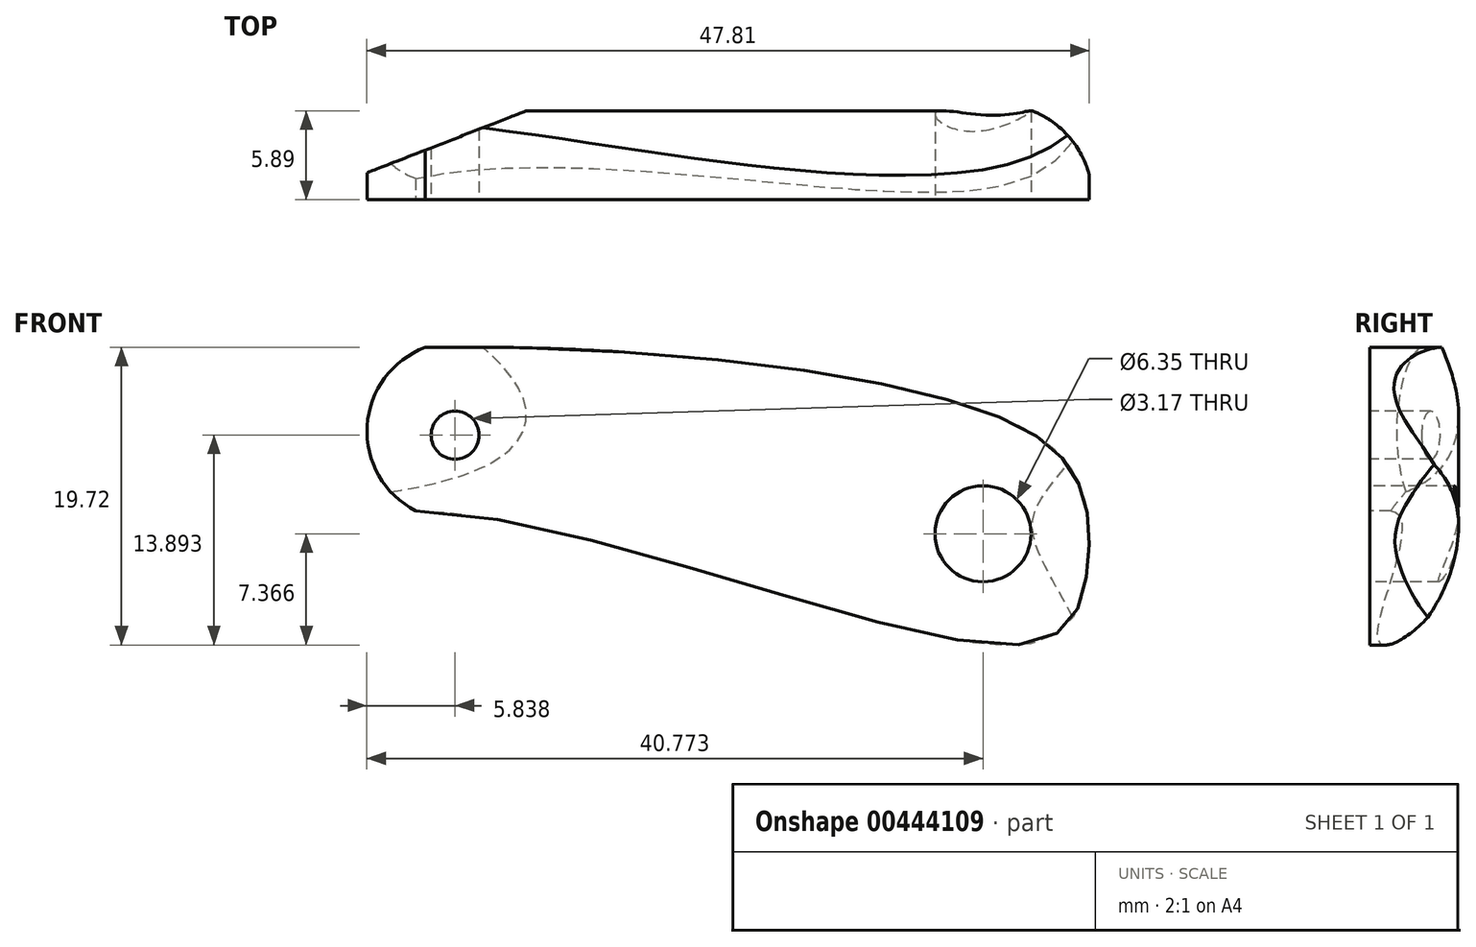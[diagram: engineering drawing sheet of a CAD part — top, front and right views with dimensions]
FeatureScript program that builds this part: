
annotation { "Feature Type Name" : "Feature", "Feature Type Description" : "" }
export const myFeature = defineFeature(function(context is Context, id is Id, definition is map)
    precondition{}
    {
        {
            var Q0;
            Q0=qCreatedBy(makeId("Front.planeOp"),FACE);
            var sketch = newSketch(context, id + "F0", { "sketchPlane" : qUnion([Q0])});
            skLineSegment(sketch, "E0", {"start": v(-1, 2.9) * mm, "end": v(0.18, 2.97) * mm});
            skPoint(sketch, "E1", {"position": v(48.62, 15.19) * mm});
            skPoint(sketch, "E2", {"position": v(13.69, 21.71) * mm});
            skArc(sketch, "E3", {"start": v(11.72, 27.52) * mm, "mid": v(7.86, 22.32) * mm, "end": v(11.07, 16.7) * mm});
            skFitSpline(sketch, "E4.trimOffspring", {"points": [v(-46.68, 0) * mm, v(-36.83, 14.74) * mm, v(0, 26.85) * mm, v(48.1, 23.51) * mm, v(54.92, 18.58) * mm, v(55.49, 12.52) * mm, v(51.4, 7.87) * mm, v(7.3, 16.37) * mm, v(0, 0) * mm], "startDerivative": vector(72.96, 165.42) * mm, "endDerivative": vector(-10.36, -190.7) * mm});
            skPoint(sketch, "E5.start.orphan", {"position": v(-1, 2.9) * mm});
            skPoint(sketch, "E6.start.orphan", {"position": v(-1.9, 17.09) * mm});
            skPoint(sketch, "E7.end.orphan", {"position": v(15.24, 75.7) * mm});
            skLineSegment(sketch, "E8", {"start": v(11.07, 16.7) * mm, "end": v(51.4, 7.87) * mm, "construction": true});
            skLineSegment(sketch, "E9", {"start": v(51.4, 7.87) * mm, "end": v(59.51, 44.88) * mm, "construction": true});
            skSolve(sketch);
        }
        {
            var Q0;
            Q0=makeQuery(id+"F0.imprint","IMPRINT",FACE,{"disambiguationData":[TD([[makeQuery(id+"F0.imprint","IMPRINT",EDGE,{"derivedFrom":sQuery(id+"F0.wireOp",EDGE,"E3")}),1.0]])]});
            extrude(context, id + "F1", {"entities" : qUnion([Q0]), "oppositeDirection" : true, "depth" : 6.35 * mm, "offsetDistance" : 25.4 * mm});
        }
        {
            var Q0;
            Q0=sQuery(id+"F0.wireOp",VERTEX,"E1");
            var Q1;
            Q1=makeQuery(id+"F1.opExtrude","SWEPT_BODY",BODY,{"disambiguationData":[OSD([sQuery(id+"F0.wireOp",EDGE,"E3"),sQuery(id+"F0.wireOp",EDGE,"E4.trimOffspring")])]});
            var Q2;
            Q2=makeQuery(id+"F1.opExtrude","SWEPT_BODY",BODY,{"disambiguationData":[OSD([sQuery(id+"F0.wireOp",EDGE,"E3"),sQuery(id+"F0.wireOp",EDGE,"E4.trimOffspring")])]});
            hole(context, id + "F2", {"style" : HoleStyle.SIMPLE, "endStyle" : HoleEndStyle.THROUGH, "holeDiameter" : 6.35 * mm, "isTappedThrough" : true, "tappedDepth" : 12.7 * mm, "tapClearance" : 3, "locations" : qUnion([Q0]), "scope" : qUnion([Q1, Q2])});
        }
        {
            var Q0;
            Q0=sQuery(id+"F0.wireOp",VERTEX,"E2");
            var Q1;
            Q1=makeQuery(id+"F1.opExtrude","SWEPT_BODY",BODY,{"disambiguationData":[OSD([sQuery(id+"F0.wireOp",EDGE,"E3"),sQuery(id+"F0.wireOp",EDGE,"E4.trimOffspring")])]});
            hole(context, id + "F3", {"style" : HoleStyle.SIMPLE, "endStyle" : HoleEndStyle.THROUGH, "holeDiameter" : 3.17 * mm, "isTappedThrough" : true, "tappedDepth" : 12.7 * mm, "tapClearance" : 3, "locations" : qUnion([Q0]), "scope" : qUnion([Q1])});
        }
        {
            var Q0;
            Q0=sQuery(id+"F0.wireOp",EDGE,"E9");
            var Q1;
            Q1=qCreatedBy(makeId("Right.planeOp"),FACE);
            cPlane(context, id + "F4", {"entities" : qUnion([Q0, Q1]), "cplaneType" : CPlaneType.LINE_ANGLE, "offset" : 25.4 * mm, "angle" : 0 * degree, "width" : 152.4 * mm, "height" : 152.4 * mm});
        }
        {
            var Q0;
            Q0=qCreatedBy(id+"F4.planeOp",FACE);
            var sketch = newSketch(context, id + "F5", { "sketchPlane" : qUnion([Q0])});
            skLineSegment(sketch, "E10", {"start": v(0, 14.17) * mm, "end": v(0, 44.65) * mm});
            skLineSegment(sketch, "E11.bottom", {"start": v(-13.26, 16.68) * mm, "end": v(13.26, 16.68) * mm});
            skLineSegment(sketch, "E11.top", {"start": v(-13.26, 37.07) * mm, "end": v(13.26, 37.07) * mm});
            skLineSegment(sketch, "E11.left", {"start": v(-13.26, 16.68) * mm, "end": v(-13.26, 37.07) * mm});
            skLineSegment(sketch, "E11.right", {"start": v(13.26, 16.68) * mm, "end": v(13.26, 37.07) * mm});
            skPoint(sketch, "E11.middle", {"position": v(0, 26.87) * mm});
            skPoint(sketch, "E12", {"position": v(0, 9.1) * mm});
            skLineSegment(sketch, "E13", {"start": v(0, 14.17) * mm, "end": v(0, 9.1) * mm});
            skLineSegment(sketch, "E14.top", {"start": v(13.26, 10.15) * mm, "end": v(-13.26, 10.15) * mm});
            skLineSegment(sketch, "E14.left", {"start": v(13.26, 16.68) * mm, "end": v(13.26, 10.15) * mm});
            skLineSegment(sketch, "E14.right", {"start": v(-13.26, 16.68) * mm, "end": v(-13.26, 10.15) * mm});
            skFitSpline(sketch, "E15", {"points": [v(0, 34.75) * mm, v(4.18, 31.05) * mm, v(5.88, 26.87) * mm, v(4.57, 22.12) * mm, v(0, 17.61) * mm], "startDerivative": vector(18.03, -13.57) * mm, "endDerivative": vector(-19.34, -14.01) * mm});
            skFitSpline(sketch, "E16.MirrorCS", {"points": [v(0, 34.75) * mm, v(-4.18, 31.05) * mm, v(-5.88, 26.87) * mm, v(-4.57, 22.12) * mm, v(0, 17.61) * mm], "startDerivative": vector(-18.03, -13.57) * mm, "endDerivative": vector(19.34, -14.01) * mm});
            skSolve(sketch);
        }
        {
            var Q0;
            {var subQ4=sQuery(id+"F5.wireOp",EDGE,"E11.left");Q0=makeQuery(id+"F5.imprint","IMPRINT",FACE,{"disambiguationData":[TD([[makeQuery(id+"F5.imprint","IMPRINT",EDGE,{"derivedFrom":subQ4}),-1.0]])]});}
            extrude(context, id + "F6", {"entities" : qUnion([Q0]), "operationType" : NewBodyOperationType.REMOVE, "endBound" : BoundingType.SYMMETRIC, "depth" : 127 * mm, "offsetDistance" : 25.4 * mm});
        }
        {
            var Q0;
            Q0=qCreatedBy(makeId("Top.planeOp"),FACE);
            var sketch = newSketch(context, id + "F7", { "sketchPlane" : qUnion([Q0])});
            skLineSegment(sketch, "E17", {"start": v(3.25, 0) * mm, "end": v(22.75, -7.58) * mm});
            skLineSegment(sketch, "E18", {"start": v(0, 0) * mm, "end": v(30.44, 0) * mm});
            skLineSegment(sketch, "E19.MirrorCS", {"start": v(3.25, 0) * mm, "end": v(22.75, 7.58) * mm});
            skLineSegment(sketch, "E20.bottom", {"start": v(0, -11.84) * mm, "end": v(16.71, -11.84) * mm});
            skLineSegment(sketch, "E20.top", {"start": v(0, 10.52) * mm, "end": v(16.71, 10.52) * mm});
            skLineSegment(sketch, "E20.left", {"start": v(0, -11.84) * mm, "end": v(0, 10.52) * mm});
            skLineSegment(sketch, "E21", {"start": v(16.71, 10.52) * mm, "end": v(21.9, 10.52) * mm});
            skLineSegment(sketch, "E22", {"start": v(21.9, 10.52) * mm, "end": v(22.39, -11.84) * mm});
            skLineSegment(sketch, "E23", {"start": v(22.39, -11.84) * mm, "end": v(16.71, -11.84) * mm});
            skCircle(sketch, "E24", {"center": v(49.53, 0) * mm, "radius": 6.35 * mm});
            skLineSegment(sketch, "E25.bottom", {"start": v(49.53, 0) * mm, "end": v(57.87, 0) * mm});
            skLineSegment(sketch, "E25.top", {"start": v(49.53, 8.85) * mm, "end": v(57.87, 8.85) * mm});
            skLineSegment(sketch, "E25.left", {"start": v(49.53, 0) * mm, "end": v(49.53, 8.85) * mm});
            skLineSegment(sketch, "E25.right", {"start": v(57.87, 0) * mm, "end": v(57.87, 8.85) * mm});
            skSolve(sketch);
        }
        {
            var Q0;
            {var subQ3=sQuery(id+"F7.wireOp",EDGE,"E20.top");Q0=makeQuery(id+"F7.imprint","IMPRINT",FACE,{"disambiguationData":[TD([[makeQuery(id+"F7.imprint","IMPRINT",EDGE,{"derivedFrom":subQ3}),-1.0]])]});}
            var Q1;
            {var subQ1=sQuery(id+"F7.wireOp",EDGE,"E25.top");Q1=makeQuery(id+"F7.imprint","IMPRINT",FACE,{"disambiguationData":[TD([[makeQuery(id+"F7.imprint","IMPRINT",EDGE,{"derivedFrom":subQ1}),-1.0]])]});}
            extrude(context, id + "F8", {"entities" : qUnion([Q0, Q1]), "operationType" : NewBodyOperationType.REMOVE, "endBound" : BoundingType.SYMMETRIC, "oppositeDirection" : true, "depth" : 76.2 * mm, "offsetDistance" : 25.4 * mm});
        }
    });
